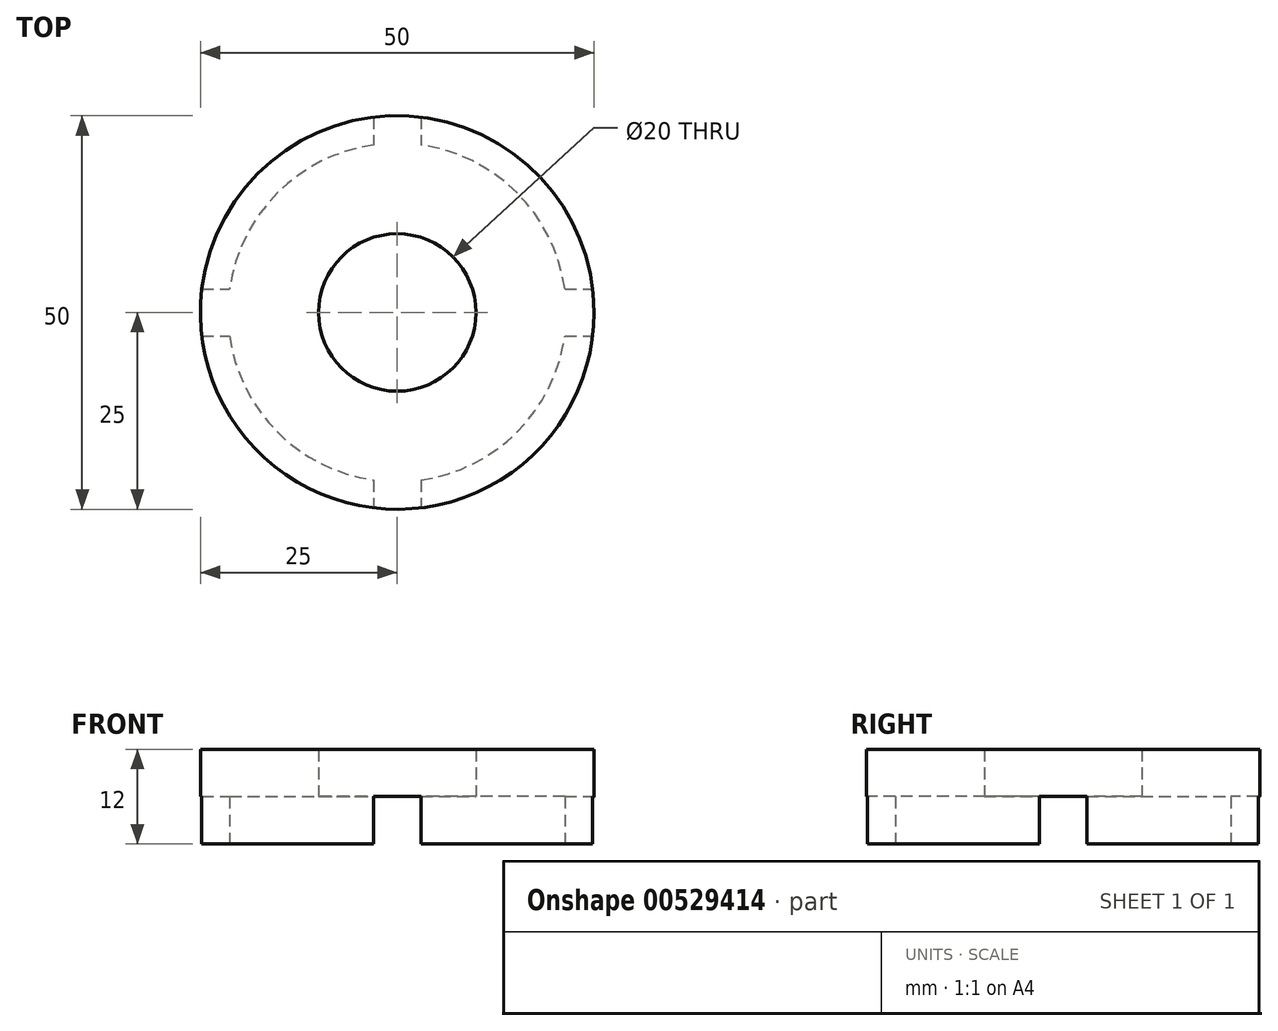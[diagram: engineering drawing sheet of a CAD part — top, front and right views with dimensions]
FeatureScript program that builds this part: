
annotation { "Feature Type Name" : "Feature", "Feature Type Description" : "" }
export const myFeature = defineFeature(function(context is Context, id is Id, definition is map)
    precondition{}
    {
        {
            var Q0;
            Q0=qCreatedBy(makeId("Top.planeOp"),FACE);
            var sketch = newSketch(context, id + "F0", { "sketchPlane" : qUnion([Q0])});
            skCircle(sketch, "E0", {"center": v(0, 0) * mm, "radius": 10 * mm});
            skCircle(sketch, "E1", {"center": v(0, 0) * mm, "radius": 25 * mm});
            skCircle(sketch, "E2", {"center": v(0, 0) * mm, "radius": 21.5 * mm});
            skLineSegment(sketch, "E3", {"start": v(0, 25) * mm, "end": v(0, -25) * mm, "construction": true});
            skLineSegment(sketch, "E4.0", {"start": v(-3, 25) * mm, "end": v(-3, 21.29) * mm});
            skLineSegment(sketch, "E5.0", {"start": v(3, 25) * mm, "end": v(3, 21.29) * mm});
            skLineSegment(sketch, "E6", {"start": v(-3, -21.29) * mm, "end": v(-3, -25) * mm});
            skLineSegment(sketch, "E7", {"start": v(-3, 21.29) * mm, "end": v(-3, -21.29) * mm, "construction": true});
            skLineSegment(sketch, "E8", {"start": v(3, 21.29) * mm, "end": v(3, -21.29) * mm, "construction": true});
            skLineSegment(sketch, "E9", {"start": v(3, -21.29) * mm, "end": v(3, -25) * mm});
            skLineSegment(sketch, "E10", {"start": v(-25, 0) * mm, "end": v(25, 0) * mm, "construction": true});
            skPoint(sketch, "E10.endSnap0", {"position": v(3, 0) * mm});
            skLineSegment(sketch, "E11.0", {"start": v(-25, -3) * mm, "end": v(-21.29, -3) * mm});
            skLineSegment(sketch, "E12.0", {"start": v(-25, 3) * mm, "end": v(-21.29, 3) * mm});
            skLineSegment(sketch, "E13", {"start": v(-21.29, -3) * mm, "end": v(21.29, -3) * mm, "construction": true});
            skLineSegment(sketch, "E14", {"start": v(-21.29, 3) * mm, "end": v(21.29, 3) * mm, "construction": true});
            skLineSegment(sketch, "E15", {"start": v(21.29, 3) * mm, "end": v(25, 3) * mm});
            skLineSegment(sketch, "E16", {"start": v(21.29, -3) * mm, "end": v(25, -3) * mm});
            skSolve(sketch);
        }
        {
            var Q0;
            Q0=makeQuery(id+"F0.imprint","IMPRINT",FACE,{"disambiguationData":[TD([[makeQuery(id+"F0.imprint","IMPRINT",EDGE,{"derivedFrom":sQuery(id+"F0.wireOp",EDGE,"E0")}),-1.0]])]});
            var Q1;
            Q1=makeQuery(id+"F0.imprint","IMPRINT",FACE,{"disambiguationData":[TD([[makeQuery(id+"F0.imprint","IMPRINT",EDGE,{"derivedFrom":sQuery(id+"F0.wireOp",EDGE,"E1")}),1.0]])]});
            extrude(context, id + "F1", {"entities" : qUnion([Q0, Q1]), "depth" : 12 * mm, "offsetDistance" : 25 * mm});
        }
        {
            var Q0;
            Q0=makeQuery(id+"F0.imprint","IMPRINT",FACE,{"disambiguationData":[TD([[makeQuery(id+"F0.imprint","IMPRINT",EDGE,{"derivedFrom":sQuery(id+"F0.wireOp",EDGE,"E0")}),-1.0]])]});
            extrude(context, id + "F2", {"entities" : qUnion([Q0]), "operationType" : NewBodyOperationType.REMOVE, "depth" : 6 * mm, "offsetDistance" : 25 * mm});
        }
        {
            var Q0;
            {var subQ0=sQuery(id+"F0.wireOp",EDGE,"E4.0");var subQ1=sQuery(id+"F0.wireOp",EDGE,"E1");var subQ2=makeQuery(id+"F0.imprint","INTERSECT",VERTEX,{"derivedFrom":[subQ1,subQ0]});Q0=makeQuery(id+"F0.imprint","IMPRINT",FACE,{"disambiguationData":[TD([[makeQuery(id+"F0.imprint","IMPRINT",EDGE,{"disambiguationData":[TD([[subQ2,1.0]])],"derivedFrom":subQ1}),1.0]])]});}
            var Q1;
            {var subQ0=sQuery(id+"F0.wireOp",EDGE,"E6");var subQ1=sQuery(id+"F0.wireOp",EDGE,"E1");var subQ2=makeQuery(id+"F0.imprint","INTERSECT",VERTEX,{"derivedFrom":[subQ1,subQ0]});Q1=makeQuery(id+"F0.imprint","IMPRINT",FACE,{"disambiguationData":[TD([[makeQuery(id+"F0.imprint","IMPRINT",EDGE,{"disambiguationData":[TD([[subQ2,-1.0]])],"derivedFrom":subQ1}),1.0]])]});}
            var Q2;
            {var subQ0=sQuery(id+"F0.wireOp",EDGE,"E12.0");var subQ1=sQuery(id+"F0.wireOp",EDGE,"E1");var subQ2=makeQuery(id+"F0.imprint","INTERSECT",VERTEX,{"derivedFrom":[subQ1,subQ0]});Q2=makeQuery(id+"F0.imprint","IMPRINT",FACE,{"disambiguationData":[TD([[makeQuery(id+"F0.imprint","IMPRINT",EDGE,{"disambiguationData":[TD([[subQ2,-1.0]])],"derivedFrom":subQ1}),1.0]])]});}
            var Q3;
            {var subQ0=sQuery(id+"F0.wireOp",EDGE,"E15");var subQ1=sQuery(id+"F0.wireOp",EDGE,"E1");var subQ2=makeQuery(id+"F0.imprint","INTERSECT",VERTEX,{"derivedFrom":[subQ1,subQ0]});Q3=makeQuery(id+"F0.imprint","IMPRINT",FACE,{"disambiguationData":[TD([[makeQuery(id+"F0.imprint","IMPRINT",EDGE,{"disambiguationData":[TD([[subQ2,1.0]])],"derivedFrom":subQ1}),1.0]])]});}
            extrude(context, id + "F3", {"entities" : qUnion([Q0, Q1, Q2, Q3]), "operationType" : NewBodyOperationType.REMOVE, "depth" : 6 * mm, "offsetDistance" : 25 * mm});
        }
    });
